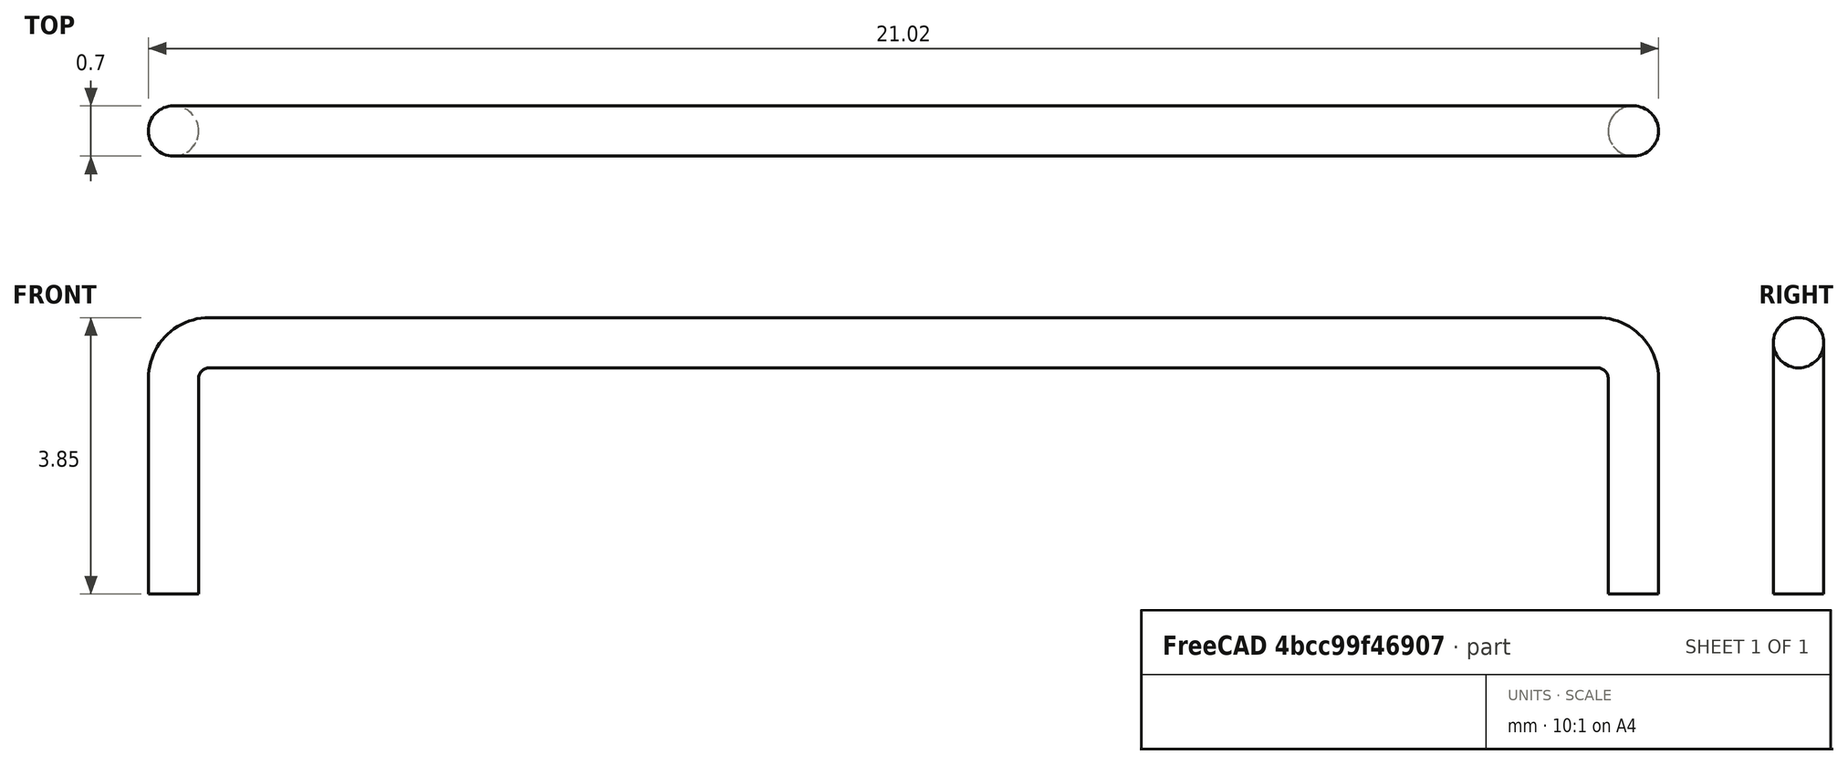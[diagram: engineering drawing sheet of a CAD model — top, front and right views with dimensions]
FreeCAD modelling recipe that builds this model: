
FCSTD DOCUMENT  (FreeCAD 0.18.4R)
Label: drahtbruecke_0.7mm_p20.32mm
License: All rights reserved
LicenseURL: http://en.wikipedia.org/wiki/All_rights_reserved
objects: Sketcher::SketchObject×2, PartDesign::AdditivePipe×1, PartDesign::Body×1
note: 5 computed .brp shape members not serialized (recipe doc carries the construction recipe); baked Part::Feature solids carry a one-line shape summary decoded from their .brp

FEATURE [Sketcher::SketchObject] Sketch
  MapMode = 5
  Placement = pos=(0,0,0) rot=(1,0,0;1.5708rad)
  Support = -> [XZ_Plane]
  sketch-geometry (5):
    g0: LineSegment StartX=0 StartY=0 StartZ=0 EndX=0 EndY=3 EndZ=0
    g1: LineSegment StartX=0.5 StartY=3.5 StartZ=0 EndX=19.82 EndY=3.5 EndZ=0
    g2: LineSegment StartX=20.32 StartY=3 StartZ=0 EndX=20.32 EndY=0 EndZ=0
    g3: ArcOfCircle CenterX=0.5 CenterY=3 CenterZ=0 NormalX=0 NormalY=0 NormalZ=1 AngleXU=0 Radius=0.5 StartAngle=1.5708 EndAngle=3.14159
    g4: ArcOfCircle CenterX=19.82 CenterY=3 CenterZ=0 NormalX=0 NormalY=0 NormalZ=1 AngleXU=0 Radius=0.5 StartAngle=0 EndAngle=1.5708
  constraints (13):
    c: Vertical(g0)
    c: Vertical(g2)
    c: Horizontal(g1)
    c: Horizontal(g2,g0)
    c: Coincident(g0,g-1)
    c: Tangent(g0,g3) = 1.5708
    c: Tangent(g1,g3) = 1.5708
    c: Tangent(g1,g4) = 1.5708
    c: Tangent(g2,g4) = 1.5708
    c: Radius(g3) = 0.5
    c: Equal(g4,g3)
    c: Distance(g0,g2) = 20.32
    c: Distance(g2) = 3
FEATURE [Sketcher::SketchObject] Sketch001
  MapMode = 5
  Support = -> [XY_Plane]
  sketch-geometry (1):
    g0: Circle CenterX=0 CenterY=0 CenterZ=0 NormalX=0 NormalY=0 NormalZ=1 AngleXU=0 Radius=0.35
  constraints (2):
    c: Coincident(g0,g-1)
    c: Radius(g0) = 0.35
FEATURE [PartDesign::AdditivePipe] AdditivePipe
  AuxilleryCurvelinear = true
  AuxillerySpineTangent = false
  Binormal = (0,0,0)
  Mode = 0
  Profile = -> Sketch001
  Spine = -> Sketch [Edge1,Edge2,Edge3,Edge4,Edge5]
  SpineTangent = false
  Transformation = 0
  Transition = 0
FEATURE [PartDesign::Body] Body
  Group = -> [Sketch,Sketch001,AdditivePipe]
  Origin = -> Origin
  Tip = -> AdditivePipe
